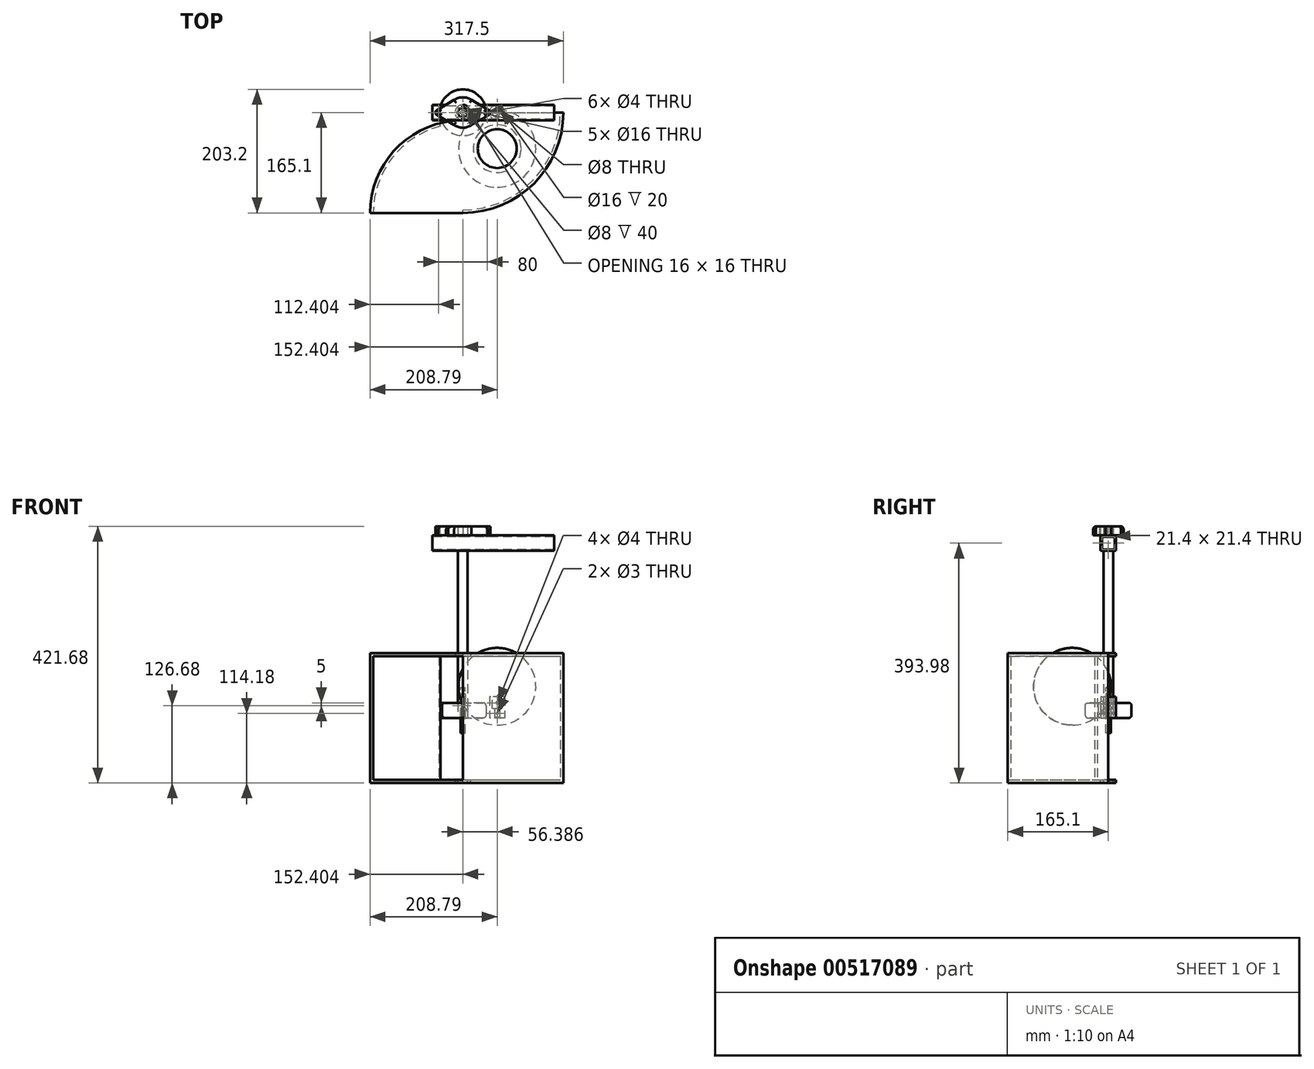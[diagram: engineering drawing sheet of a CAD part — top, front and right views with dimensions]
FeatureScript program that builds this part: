
annotation { "Feature Type Name" : "Feature", "Feature Type Description" : "" }
export const myFeature = defineFeature(function(context is Context, id is Id, definition is map)
    precondition{}
    {
        {
            var Q0;
            Q0=qCreatedBy(makeId("Top.planeOp"),FACE);
            var sketch = newSketch(context, id + "F0", { "sketchPlane" : qUnion([Q0])});
            skCircle(sketch, "E0", {"center": v(0, 0) * mm, "radius": 4 * mm});
            skCircle(sketch, "E1", {"center": v(0, 0) * mm, "radius": 12.5 * mm});
            skSolve(sketch);
        }
        {
            var Q0;
            Q0 = qSketchRegion(id + "F0", true);
            extrude(context, id + "F1", {"entities" : qUnion([Q0]), "depth" : 35 * mm, "offsetDistance" : 25 * mm});
        }
        {
            var Q0;
            Q0=makeQuery(id+"F1.opExtrude","CAP_FACE",FACE,{"disambiguationData":[OSD([sQuery(id+"F0.wireOp",EDGE,"E0"),sQuery(id+"F0.wireOp",EDGE,"E1")])],"isStart":false});
            var sketch = newSketch(context, id + "F2", { "sketchPlane" : qUnion([Q0])});
            skCircle(sketch, "E2", {"center": v(0, 0) * mm, "radius": 8 * mm});
            skSolve(sketch);
        }
        {
            var Q0;
            Q0 = qSketchRegion(id + "F2", true);
            extrude(context, id + "F3", {"entities" : qUnion([Q0]), "operationType" : NewBodyOperationType.REMOVE, "oppositeDirection" : true, "depth" : 20 * mm, "offsetDistance" : 25 * mm});
        }
        {
            var Q0;
            Q0=qCreatedBy(makeId("Right.planeOp"),FACE);
            cPlane(context, id + "F4", {"entities" : qUnion([Q0]), "cplaneType" : CPlaneType.OFFSET, "offset" : 0 * mm, "width" : 150 * mm, "height" : 150 * mm});
        }
        {
            var Q0;
            Q0=qCreatedBy(makeId("Front.planeOp"),FACE);
            var sketch = newSketch(context, id + "F5", { "sketchPlane" : qUnion([Q0])});
            skLineSegment(sketch, "E3.0", {"start": v(-12.5, 35) * mm, "end": v(12.5, 35) * mm});
            skLineSegment(sketch, "E4.0", {"start": v(-4, 0) * mm, "end": v(4, 0) * mm});
            skLineSegment(sketch, "E5", {"start": v(0, 0) * mm, "end": v(0, 35) * mm});
            skLineSegment(sketch, "E6", {"start": v(0, 35) * mm, "end": v(0, 25) * mm});
            skLineSegment(sketch, "E7", {"start": v(0, 0) * mm, "end": v(0, 7.5) * mm});
            skCircle(sketch, "E8", {"center": v(0, 7.5) * mm, "radius": 1.5 * mm});
            skCircle(sketch, "E9", {"center": v(0, 25) * mm, "radius": 2 * mm});
            skSolve(sketch);
        }
        {
            var Q0;
            Q0 = qSketchRegion(id + "F5", true);
            extrude(context, id + "F6", {"entities" : qUnion([Q0]), "operationType" : NewBodyOperationType.REMOVE, "oppositeDirection" : true, "depth" : 25 * mm, "offsetDistance" : 25 * mm, "hasSecondDirection" : true, "secondDirectionOppositeDirection" : false, "secondDirectionDepth" : 25 * mm});
        }
        {
            var Q0;
            Q0=makeQuery(id+"F1.opExtrude","CAP_EDGE",EDGE,{"disambiguationData":[OSD([sQuery(id+"F0.wireOp",EDGE,"E0")])],"isStart":true});
            var Q1;
            Q1=makeQuery(id+"F3.boolean.opBoolean","COPY",EDGE,{"derivedFrom":makeQuery(id+"F3.opExtrude","CAP_EDGE",EDGE,{"disambiguationData":[OSD([sQuery(id+"F2.wireOp",EDGE,"E2")])],"isStart":true})});
            chamfer(context, id + "F7", {"entities" : qUnion([Q0, Q1]), "width" : 1 * mm, "tangentPropagation" : true});
        }
        {
            var Q0;
            Q0=qCreatedBy(makeId("Top.planeOp"),FACE);
            var sketch = newSketch(context, id + "F8", { "sketchPlane" : qUnion([Q0])});
            skCircle(sketch, "E10", {"center": v(-56.39, 0) * mm, "radius": 8 * mm});
            skSolve(sketch);
        }
        {
            var Q0;
            Q0 = qSketchRegion(id + "F8", true);
            extrude(context, id + "F9", {"entities" : qUnion([Q0]), "depth" : 300 * mm, "offsetDistance" : 25 * mm});
        }
        {
            var Q0;
            Q0=makeQuery(id+"F9.opExtrude","CAP_FACE",FACE,{"disambiguationData":[OSD([sQuery(id+"F8.wireOp",EDGE,"E10")])],"isStart":true});
            var sketch = newSketch(context, id + "F10", { "sketchPlane" : qUnion([Q0])});
            skCircle(sketch, "E11", {"center": v(-56.39, 0) * mm, "radius": 4 * mm});
            skSolve(sketch);
        }
        {
            var Q0;
            Q0 = qSketchRegion(id + "F10", true);
            extrude(context, id + "F11", {"entities" : qUnion([Q0]), "operationType" : NewBodyOperationType.REMOVE, "oppositeDirection" : true, "depth" : 40 * mm, "offsetDistance" : 25 * mm});
        }
        {
            var Q0;
            Q0=qCreatedBy(makeId("Front.planeOp"),FACE);
            var sketch = newSketch(context, id + "F12", { "sketchPlane" : qUnion([Q0])});
            skLineSegment(sketch, "E12.0", {"start": v(-64.39, 0) * mm, "end": v(-48.39, 0) * mm});
            skLineSegment(sketch, "E13", {"start": v(-56.39, 0) * mm, "end": v(-56.39, 20) * mm});
            skCircle(sketch, "E14", {"center": v(-56.39, 20) * mm, "radius": 2 * mm});
            skSolve(sketch);
        }
        {
            var Q0;
            Q0 = qSketchRegion(id + "F12", true);
            extrude(context, id + "F13", {"entities" : qUnion([Q0]), "operationType" : NewBodyOperationType.REMOVE, "oppositeDirection" : true, "depth" : 25 * mm, "offsetDistance" : 25 * mm, "hasSecondDirection" : true, "secondDirectionOppositeDirection" : false, "secondDirectionDepth" : 25 * mm});
        }
        {
            var Q0;
            Q0=makeQuery(id+"F9.opExtrude","CAP_FACE",FACE,{"disambiguationData":[OSD([sQuery(id+"F8.wireOp",EDGE,"E10")])],"isStart":true});
            var sketch = newSketch(context, id + "F14", { "sketchPlane" : qUnion([Q0])});
            skCircle(sketch, "E15", {"center": v(-56.39, 0) * mm, "radius": 3.94 * mm});
            skSolve(sketch);
        }
        {
            var Q0;
            Q0 = qSketchRegion(id + "F14", true);
            extrude(context, id + "F15", {"entities" : qUnion([Q0]), "depth" : 25 * mm, "offsetDistance" : 25 * mm, "hasSecondDirection" : true, "secondDirectionOppositeDirection" : true, "secondDirectionDepth" : 50 * mm});
        }
        {
            var Q0;
            Q0=qCreatedBy(makeId("Top.planeOp"),FACE);
            var sketch = newSketch(context, id + "F16", { "sketchPlane" : qUnion([Q0])});
            skCircle(sketch, "E16.0", {"center": v(-56.39, 0) * mm, "radius": 8 * mm});
            skCircle(sketch, "E17", {"center": v(-56.39, 0) * mm, "radius": 38.1 * mm});
            skSolve(sketch);
        }
        {
            var Q0;
            Q0 = qSketchRegion(id + "F16", true);
            extrude(context, id + "F17", {"entities" : qUnion([Q0]), "depth" : 25 * mm, "offsetDistance" : 25 * mm});
        }
        {
            var Q0;
            Q0=makeQuery(id+"F17.opExtrude","CAP_EDGE",EDGE,{"disambiguationData":[OSD([sQuery(id+"F16.wireOp",EDGE,"E17")])],"isStart":false});
            var Q1;
            Q1=makeQuery(id+"F17.opExtrude","CAP_EDGE",EDGE,{"disambiguationData":[OSD([sQuery(id+"F16.wireOp",EDGE,"E17")])],"isStart":true});
            fillet(context, id + "F18", {"entities" : qUnion([Q0, Q1]), "radius" : 5 * mm, "tangentPropagation" : true, "allowEdgeOverflow" : false});
        }
        {
            var Q0;
            Q0=makeQuery(id+"F9.opExtrude","CAP_FACE",FACE,{"disambiguationData":[OSD([sQuery(id+"F8.wireOp",EDGE,"E10")])],"isStart":false});
            var sketch = newSketch(context, id + "F19", { "sketchPlane" : qUnion([Q0])});
            skCircle(sketch, "E18.0", {"center": v(-56.39, 0) * mm, "radius": 8 * mm});
            skCircle(sketch, "E19", {"center": v(-56.39, 0) * mm, "radius": 13.3 * mm});
            skLineSegment(sketch, "E20", {"start": v(-56.39, 0) * mm, "end": v(-96.39, 0) * mm});
            skLineSegment(sketch, "E21", {"start": v(-96.39, 0) * mm, "end": v(-56.39, 0) * mm});
            skLineSegment(sketch, "E22", {"start": v(-56.39, 0) * mm, "end": v(-16.39, 0) * mm});
            skCircle(sketch, "E23", {"center": v(-16.39, 0) * mm, "radius": 5 * mm});
            skCircle(sketch, "E24", {"center": v(-96.39, 0) * mm, "radius": 5 * mm});
            skCircle(sketch, "E25", {"center": v(-56.39, 0) * mm, "radius": 25 * mm});
            skLineSegment(sketch, "E26", {"start": v(-42.15, -20.55) * mm, "end": v(-15.67, -4.95) * mm});
            skLineSegment(sketch, "E27", {"start": v(-56.39, 0) * mm, "end": v(-56.39, -25) * mm});
            skLineSegment(sketch, "E28.MirrorCS", {"start": v(-70.62, -20.55) * mm, "end": v(-97.1, -4.95) * mm});
            skLineSegment(sketch, "E29.MirrorCS", {"start": v(-70.62, 20.55) * mm, "end": v(-97.1, 4.95) * mm});
            skLineSegment(sketch, "E30.MirrorCS", {"start": v(-42.15, 20.55) * mm, "end": v(-15.67, 4.95) * mm});
            skCircle(sketch, "E31", {"center": v(-16.39, 0) * mm, "radius": 2 * mm});
            skCircle(sketch, "E32", {"center": v(-96.39, 0) * mm, "radius": 2 * mm});
            skSolve(sketch);
        }
        {
            var Q0;
            Q0 = qSketchRegion(id + "F19", true);
            var Q1;
            {var subQ0=sQuery(id+"F19.wireOp",EDGE,"E21");var subQ1=sQuery(id+"F19.wireOp",EDGE,"E18.0");var subQ2=makeQuery(id+"F19.imprint","INTERSECT",VERTEX,{"derivedFrom":[subQ1,subQ0]});Q1=makeQuery(id+"F19.imprint","IMPRINT",FACE,{"disambiguationData":[TD([[makeQuery(id+"F19.imprint","IMPRINT",EDGE,{"disambiguationData":[TD([[subQ2,-1.0]])],"derivedFrom":subQ1}),-1.0]])]});}
            var Q2;
            {var subQ0=sQuery(id+"F19.wireOp",EDGE,"E21");var subQ1=sQuery(id+"F19.wireOp",EDGE,"E18.0");var subQ2=makeQuery(id+"F19.imprint","INTERSECT",VERTEX,{"derivedFrom":[subQ1,subQ0]});Q2=makeQuery(id+"F19.imprint","IMPRINT",FACE,{"disambiguationData":[TD([[makeQuery(id+"F19.imprint","IMPRINT",EDGE,{"disambiguationData":[TD([[subQ2,1.0]])],"derivedFrom":subQ1}),-1.0]])]});}
            var Q3;
            {var subQ0=sQuery(id+"F19.wireOp",EDGE,"E22");var subQ1=sQuery(id+"F19.wireOp",EDGE,"E18.0");var subQ2=makeQuery(id+"F19.imprint","INTERSECT",VERTEX,{"derivedFrom":[subQ1,subQ0]});Q3=makeQuery(id+"F19.imprint","IMPRINT",FACE,{"disambiguationData":[TD([[makeQuery(id+"F19.imprint","IMPRINT",EDGE,{"disambiguationData":[TD([[subQ2,1.0]])],"derivedFrom":subQ1}),-1.0]])]});}
            extrude(context, id + "F20", {"entities" : qUnion([Q0, Q1, Q2, Q3]), "depth" : 15 * mm, "offsetDistance" : 25 * mm});
        }
        {
            var Q0;
            Q0=makeQuery(id+"F20.opExtrude","CAP_EDGE",EDGE,{"disambiguationData":[OSD([sQuery(id+"F19.wireOp",EDGE,"E28.MirrorCS")])],"isStart":false});
            var Q1;
            Q1=makeQuery(id+"F20.opExtrude","CAP_EDGE",EDGE,{"disambiguationData":[OSD([sQuery(id+"F19.wireOp",EDGE,"E26")])],"isStart":false});
            var Q2;
            Q2=makeQuery(id+"F20.opExtrude","CAP_EDGE",EDGE,{"disambiguationData":[OSD([sQuery(id+"F19.wireOp",EDGE,"E30.MirrorCS")])],"isStart":false});
            var Q3;
            Q3=makeQuery(id+"F20.opExtrude","CAP_EDGE",EDGE,{"disambiguationData":[OSD([sQuery(id+"F19.wireOp",EDGE,"E29.MirrorCS")])],"isStart":false});
            var Q4;
            {var subQ0=sQuery(id+"F19.wireOp",EDGE,"E25");Q4=makeQuery(id+"F20.opExtrude","CAP_EDGE",EDGE,{"disambiguationData":[OSD([subQ0]),TDD([makeQuery(id+"F19.imprint","IMPRINT",EDGE,{"disambiguationData":[TD([[makeQuery(id+"F19.imprint","INTERSECT",VERTEX,{"derivedFrom":[subQ0,sQuery(id+"F19.wireOp",EDGE,"E29.MirrorCS")]}),1.0]])],"derivedFrom":subQ0})])],"isStart":false});}
            var Q5;
            {var subQ0=sQuery(id+"F19.wireOp",EDGE,"E25");var subQ1=makeQuery(id+"F19.imprint","INTERSECT",VERTEX,{"derivedFrom":[subQ0,sQuery(id+"F19.wireOp",EDGE,"E27")]});Q5=makeQuery(id+"F20.opExtrude","CAP_EDGE",EDGE,{"disambiguationData":[OSD([subQ0]),TDD([makeQuery(id+"F19.imprint","IMPRINT",EDGE,{"disambiguationData":[TD([[subQ1,1.0]])],"derivedFrom":subQ0}),makeQuery(id+"F19.imprint","IMPRINT",EDGE,{"disambiguationData":[TD([[makeQuery(id+"F19.imprint","INTERSECT",VERTEX,{"derivedFrom":[subQ0,sQuery(id+"F19.wireOp",EDGE,"E26")]}),1.0]])],"derivedFrom":subQ0})])],"isStart":false});}
            fillet(context, id + "F21", {"entities" : qUnion([Q0, Q1, Q2, Q3, Q4, Q5]), "radius" : 5 * mm, "tangentPropagation" : true, "allowEdgeOverflow" : false});
        }
        {
            var Q0;
            Q0=makeQuery(id+"F20.opExtrude","CAP_FACE",FACE,{"disambiguationData":[OSD([sQuery(id+"F19.wireOp",EDGE,"E18.0"),sQuery(id+"F19.wireOp",EDGE,"E23"),sQuery(id+"F19.wireOp",EDGE,"E24"),sQuery(id+"F19.wireOp",EDGE,"E25"),sQuery(id+"F19.wireOp",EDGE,"E26"),sQuery(id+"F19.wireOp",EDGE,"E28.MirrorCS"),sQuery(id+"F19.wireOp",EDGE,"E29.MirrorCS"),sQuery(id+"F19.wireOp",EDGE,"E30.MirrorCS"),sQuery(id+"F19.wireOp",EDGE,"E31"),sQuery(id+"F19.wireOp",EDGE,"E32")])],"isStart":true});
            var sketch = newSketch(context, id + "F22", { "sketchPlane" : qUnion([Q0])});
            skCircle(sketch, "E33.0", {"center": v(-56.39, 0) * mm, "radius": 8 * mm});
            skLineSegment(sketch, "E34.bottom", {"start": v(-6.39, 12.7) * mm, "end": v(-106.39, 12.7) * mm});
            skLineSegment(sketch, "E34.top", {"start": v(-6.39, -12.7) * mm, "end": v(-106.39, -12.7) * mm});
            skLineSegment(sketch, "E34.right", {"start": v(-106.39, 12.7) * mm, "end": v(-106.39, -12.7) * mm});
            skLineSegment(sketch, "E35", {"start": v(-6.39, -12.7) * mm, "end": v(93.61, -12.7) * mm});
            skLineSegment(sketch, "E36", {"start": v(93.61, -12.7) * mm, "end": v(93.61, 12.7) * mm});
            skLineSegment(sketch, "E37", {"start": v(93.61, 12.7) * mm, "end": v(-6.39, 12.7) * mm});
            skCircle(sketch, "E38.0", {"center": v(-96.39, 0) * mm, "radius": 2 * mm});
            skCircle(sketch, "E39.0", {"center": v(-16.39, 0) * mm, "radius": 2 * mm});
            skSolve(sketch);
        }
        {
            var Q0;
            Q0 = qSketchRegion(id + "F22", true);
            extrude(context, id + "F23", {"entities" : qUnion([Q0]), "depth" : 25.4 * mm, "offsetDistance" : 25 * mm});
        }
        {
            var Q0;
            Q0=makeQuery(id+"F23.opExtrude","SWEPT_FACE",FACE,{"disambiguationData":[OSD([sQuery(id+"F22.wireOp",EDGE,"E34.right")])]});
            var sketch = newSketch(context, id + "F24", { "sketchPlane" : qUnion([Q0])});
            skLineSegment(sketch, "E40.0", {"start": v(10.7, 298) * mm, "end": v(-10.7, 298) * mm});
            skLineSegment(sketch, "E40.1", {"start": v(10.7, 276.6) * mm, "end": v(10.7, 298) * mm});
            skLineSegment(sketch, "E40.2", {"start": v(-10.7, 276.6) * mm, "end": v(10.7, 276.6) * mm});
            skLineSegment(sketch, "E40.3", {"start": v(-10.7, 298) * mm, "end": v(-10.7, 276.6) * mm});
            skSolve(sketch);
        }
        {
            var Q0;
            Q0 = qSketchRegion(id + "F24", true);
            extrude(context, id + "F25", {"entities" : qUnion([Q0]), "operationType" : NewBodyOperationType.REMOVE, "oppositeDirection" : true, "depth" : 500 * mm, "offsetDistance" : 25 * mm});
        }
        {
            var Q0;
            Q0=qCreatedBy(id+"F4.planeOp",FACE);
            var sketch = newSketch(context, id + "F26", { "sketchPlane" : qUnion([Q0])});
            skCircle(sketch, "E41", {"center": v(-59.35, 51.77) * mm, "radius": 63.5 * mm});
            skLineSegment(sketch, "E42", {"start": v(-59.35, 115.27) * mm, "end": v(-59.35, -11.73) * mm});
            skSolve(sketch);
        }
        {
            var Q0;
            {var subQ0=sQuery(id+"F26.wireOp",EDGE,"E42");Q0=makeQuery(id+"F26.imprint","IMPRINT",FACE,{"disambiguationData":[TD([[makeQuery(id+"F26.imprint","IMPRINT",EDGE,{"derivedFrom":subQ0}),1.0]])]});}
            var Q1;
            Q1=sQuery(id+"F26.wireOp",EDGE,"E42");
            revolve(context, id + "F27", {"entities" : qUnion([Q0]), "axis" : qUnion([Q1]), "revolveType" : RevolveType.FULL});
        }
        {
            var Q0;
            Q0=qCreatedBy(makeId("Top.planeOp"),FACE);
            var sketch = newSketch(context, id + "F28", { "sketchPlane" : qUnion([Q0])});
            skCircle(sketch, "E43.0", {"center": v(-56.39, 0) * mm, "radius": 38.1 * mm});
            skArc(sketch, "E44", {"start": v(-56.39, -160.02) * mm, "mid": v(56.77, -113.15) * mm, "end": v(103.63, 0) * mm});
            skArc(sketch, "E45.0", {"start": v(-56.39, -165.1) * mm, "mid": v(60.36, -116.74) * mm, "end": v(108.71, 0) * mm});
            skLineSegment(sketch, "E46", {"start": v(-56.39, 0) * mm, "end": v(-56.39, -211.07) * mm});
            skLineSegment(sketch, "E47", {"start": v(-56.39, 0) * mm, "end": v(143.2, 0) * mm});
            skSolve(sketch);
        }
        {
            var Q0;
            {var subQ0=sQuery(id+"F28.wireOp",EDGE,"E44");Q0=makeQuery(id+"F28.imprint","IMPRINT",FACE,{"disambiguationData":[TD([[makeQuery(id+"F28.imprint","IMPRINT",EDGE,{"derivedFrom":subQ0}),-1.0]])]});}
            extrude(context, id + "F29", {"entities" : qUnion([Q0]), "depth" : 101.6 * mm, "offsetDistance" : 25 * mm, "hasSecondDirection" : true, "secondDirectionOppositeDirection" : true, "secondDirectionDepth" : 101.6 * mm});
        }
        {
            var Q0;
            Q0=makeQuery(id+"F29.opExtrude","CAP_FACE",FACE,{"disambiguationData":[OSD([sQuery(id+"F28.wireOp",EDGE,"E44"),sQuery(id+"F28.wireOp",EDGE,"E45.0"),sQuery(id+"F28.wireOp",EDGE,"E46"),sQuery(id+"F28.wireOp",EDGE,"E47")])],"isStart":true});
            var sketch = newSketch(context, id + "F30", { "sketchPlane" : qUnion([Q0])});
            skCircle(sketch, "E48.0", {"center": v(-56.39, 0) * mm, "radius": 3.94 * mm});
            skLineSegment(sketch, "E49", {"start": v(-56.39, 0) * mm, "end": v(-56.39, 160.02) * mm});
            skLineSegment(sketch, "E50", {"start": v(-56.39, 0) * mm, "end": v(108.71, 0) * mm});
            skArc(sketch, "E51.0", {"start": v(-56.39, 160.02) * mm, "mid": v(56.77, 113.15) * mm, "end": v(103.63, 0) * mm});
            skArc(sketch, "E52.0", {"start": v(-56.39, 165.1) * mm, "mid": v(60.36, 116.74) * mm, "end": v(108.71, 0) * mm});
            skCircle(sketch, "E53", {"center": v(-56.39, 0) * mm, "radius": 12.7 * mm});
            skCircle(sketch, "E54.0", {"center": v(-56.39, 0) * mm, "radius": 8 * mm});
            skSolve(sketch);
        }
        {
            var Q0;
            Q0 = qSketchRegion(id + "F30", true);
            var Q1;
            {var subQ0=sQuery(id+"F30.wireOp",EDGE,"E51.0");Q1=makeQuery(id+"F30.imprint","IMPRINT",FACE,{"disambiguationData":[TD([[makeQuery(id+"F30.imprint","IMPRINT",EDGE,{"derivedFrom":subQ0}),1.0]])]});}
            extrude(context, id + "F31", {"entities" : qUnion([Q0, Q1]), "operationType" : NewBodyOperationType.ADD, "depth" : 5.08 * mm, "offsetDistance" : 25 * mm});
        }
        {
            var Q0;
            Q0=makeQuery(id+"F29.opExtrude","CAP_FACE",FACE,{"disambiguationData":[OSD([sQuery(id+"F28.wireOp",EDGE,"E44"),sQuery(id+"F28.wireOp",EDGE,"E45.0"),sQuery(id+"F28.wireOp",EDGE,"E46"),sQuery(id+"F28.wireOp",EDGE,"E47")])],"isStart":false});
            var sketch = newSketch(context, id + "F32", { "sketchPlane" : qUnion([Q0])});
            skLineSegment(sketch, "E55.0.0", {"start": v(-56.39, -12.7) * mm, "end": v(-56.39, -160.02) * mm});
            skArc(sketch, "E55.0.1", {"start": v(-56.39, -160.02) * mm, "mid": v(56.77, -113.15) * mm, "end": v(103.63, 0) * mm});
            skLineSegment(sketch, "E55.0.2", {"start": v(103.63, 0) * mm, "end": v(-43.69, 0) * mm});
            skArc(sketch, "E55.0.3", {"start": v(-43.69, 0) * mm, "mid": v(-65.37, 8.98) * mm, "end": v(-56.39, -12.7) * mm});
            skArc(sketch, "E56.0", {"start": v(-56.39, -165.1) * mm, "mid": v(60.36, -116.74) * mm, "end": v(108.71, 0) * mm});
            skLineSegment(sketch, "E57.0", {"start": v(-56.39, -160.02) * mm, "end": v(-56.39, -165.1) * mm});
            skLineSegment(sketch, "E58.0", {"start": v(103.63, 0) * mm, "end": v(108.71, 0) * mm});
            skCircle(sketch, "E59.0", {"center": v(-56.39, 0) * mm, "radius": 8 * mm});
            skSolve(sketch);
        }
        {
            var Q0;
            Q0 = qSketchRegion(id + "F32", true);
            extrude(context, id + "F33", {"entities" : qUnion([Q0]), "operationType" : NewBodyOperationType.ADD, "depth" : 5.08 * mm, "offsetDistance" : 25 * mm});
        }
        {
            var Q0;
            {var subQ0=sQuery(id+"F28.wireOp",EDGE,"E46");Q0=makeQuery(id+"F33.boolean.opBoolean","MERGE",FACE,{"derivedFrom":[makeQuery(id+"F31.boolean.opBoolean","MERGE",FACE,{"derivedFrom":[makeQuery(id+"F29.opExtrude","SWEPT_FACE",FACE,{"disambiguationData":[OSD([subQ0])]}),makeQuery(id+"F31.opExtrude","SWEPT_FACE",FACE,{"disambiguationData":[OSD([subQ0,sQuery(id+"F30.wireOp",EDGE,"E49")])]})]}),makeQuery(id+"F33.opExtrude","SWEPT_FACE",FACE,{"disambiguationData":[OSD([sQuery(id+"F32.wireOp",EDGE,"E55.0.0"),sQuery(id+"F32.wireOp",EDGE,"E57.0")])]})]});}
            extrude(context, id + "F34", {"entities" : qUnion([Q0]), "operationType" : NewBodyOperationType.ADD, "depth" : 152.4 * mm, "offsetDistance" : 25 * mm});
        }
        {
            var Q0;
            {var subQ0=sQuery(id+"F30.wireOp",EDGE,"E49");var subQ1=sQuery(id+"F28.wireOp",EDGE,"E46");Q0=makeQuery(id+"F34.boolean.opBoolean","MERGE",FACE,{"derivedFrom":[makeQuery(id+"F31.opExtrude","CAP_FACE",FACE,{"disambiguationData":[OSD([subQ1,subQ0,sQuery(id+"F30.wireOp",EDGE,"E50"),sQuery(id+"F30.wireOp",EDGE,"E52.0"),sQuery(id+"F30.wireOp",EDGE,"E53"),sQuery(id+"F30.wireOp",EDGE,"E54.0")])],"isStart":false}),makeQuery(id+"F34.opExtrude","SWEPT_FACE",FACE,{"disambiguationData":[OSD([subQ1,subQ0]),TDD([makeQuery(id+"F31.opExtrude","CAP_EDGE",EDGE,{"disambiguationData":[OSD([subQ1,subQ0])],"isStart":false})])]})]});}
            var sketch = newSketch(context, id + "F35", { "sketchPlane" : qUnion([Q0])});
            skArc(sketch, "E60.0", {"start": v(-56.39, 12.7) * mm, "mid": v(-65.37, -8.98) * mm, "end": v(-43.69, 0) * mm});
            skLineSegment(sketch, "E61", {"start": v(-56.39, 12.7) * mm, "end": v(-56.39, 203.81) * mm});
            skCircle(sketch, "E62", {"center": v(-56.39, 165.1) * mm, "radius": 152.4 * mm});
            skSolve(sketch);
        }
        {
            var Q0;
            {var subQ1=sQuery(id+"F30.wireOp",EDGE,"E49");var subQ4=sQuery(id+"F30.wireOp",EDGE,"E53");var subQ5=makeQuery(id+"F34.opExtrude","SWEPT_EDGE",EDGE,{"disambiguationData":[OSD([subQ1,subQ4]),TDD([makeQuery(id+"F31.opExtrude","CAP_VERTEX",VERTEX,{"disambiguationData":[OSD([subQ1,subQ4])],"isStart":false})])]});Q0=makeQuery(id+"F35.imprint","IMPRINT",FACE,{"disambiguationData":[TD([[makeQuery(id+"F35.imprint","IMPRINT",EDGE,{"derivedFrom":subQ5}),1.0]])]});}
            extrude(context, id + "F36", {"entities" : qUnion([Q0]), "operationType" : NewBodyOperationType.REMOVE, "oppositeDirection" : true, "depth" : 1270 * mm, "offsetDistance" : 25 * mm});
        }
        {
            var Q0;
            Q0=makeQuery(id+"F34.opExtrude","SWEPT_FACE",FACE,{"disambiguationData":[OSD([sQuery(id+"F28.wireOp",EDGE,"E44"),sQuery(id+"F28.wireOp",EDGE,"E46")])]});
            var sketch = newSketch(context, id + "F37", { "sketchPlane" : qUnion([Q0])});
            skSolve(sketch);
        }
        {
            var Q0;
            {var subQ0=sQuery(id+"F28.wireOp",EDGE,"E46");var subQ1=sQuery(id+"F28.wireOp",EDGE,"E44");Q0=makeQuery(id+"F37.imprint","IMPRINT",FACE,{"disambiguationData":[TD([[makeQuery(id+"F37.imprint","IMPRINT",EDGE,{"derivedFrom":makeQuery(id+"F34.opExtrude","SWEPT_EDGE",EDGE,{"disambiguationData":[OSD([subQ1,subQ0]),TDD([makeQuery(id+"F29.opExtrude","CAP_VERTEX",VERTEX,{"disambiguationData":[OSD([subQ1,subQ0])],"isStart":true})])]})}),-1.0]])]});}
            extrude(context, id + "F38", {"entities" : qUnion([Q0]), "operationType" : NewBodyOperationType.REMOVE, "oppositeDirection" : true, "depth" : 25 * mm, "offsetDistance" : 25 * mm});
        }
        {
            var Q0;
            {var subQ0=sQuery(id+"F30.wireOp",EDGE,"E49");var subQ1=sQuery(id+"F28.wireOp",EDGE,"E46");Q0=makeQuery(id+"F34.boolean.opBoolean","MERGE",FACE,{"derivedFrom":[makeQuery(id+"F31.opExtrude","CAP_FACE",FACE,{"disambiguationData":[OSD([subQ1,subQ0,sQuery(id+"F30.wireOp",EDGE,"E50"),sQuery(id+"F30.wireOp",EDGE,"E52.0"),sQuery(id+"F30.wireOp",EDGE,"E53"),sQuery(id+"F30.wireOp",EDGE,"E54.0")])],"isStart":false}),makeQuery(id+"F34.opExtrude","SWEPT_FACE",FACE,{"disambiguationData":[OSD([subQ1,subQ0]),TDD([makeQuery(id+"F31.opExtrude","CAP_EDGE",EDGE,{"disambiguationData":[OSD([subQ1,subQ0])],"isStart":false})])]})]});}
            var sketch = newSketch(context, id + "F39", { "sketchPlane" : qUnion([Q0])});
            skCircle(sketch, "E63.0", {"center": v(-56.39, 0) * mm, "radius": 38.1 * mm});
            skArc(sketch, "E64.0", {"start": v(-208.79, 165.1) * mm, "mid": v(-164.15, 57.34) * mm, "end": v(-56.39, 12.7) * mm});
            skArc(sketch, "E65.0", {"start": v(-203.7, 165.1) * mm, "mid": v(-160.56, 60.93) * mm, "end": v(-56.39, 17.78) * mm});
            skCircle(sketch, "E66.0", {"center": v(-56.39, 0) * mm, "radius": 43.1 * mm});
            skSolve(sketch);
        }
        {
            var Q0;
            {var subQ0=sQuery(id+"F39.wireOp",EDGE,"E64.0");var subQ3=sQuery(id+"F39.wireOp",EDGE,"E66.0");var subQ4=makeQuery(id+"F39.imprint","INTERSECT",VERTEX,{"derivedFrom":[subQ0,subQ3]});Q0=makeQuery(id+"F39.imprint","IMPRINT",FACE,{"disambiguationData":[TD([[makeQuery(id+"F39.imprint","IMPRINT",EDGE,{"disambiguationData":[TD([[subQ4,1.0]])],"derivedFrom":subQ3}),-1.0]])]});}
            var Q1;
            {var subQ0=sQuery(id+"F32.wireOp",EDGE,"E57.0");var subQ1=sQuery(id+"F32.wireOp",EDGE,"E55.0.0");Q1=makeQuery(id+"F34.boolean.opBoolean","MERGE",FACE,{"derivedFrom":[makeQuery(id+"F33.opExtrude","CAP_FACE",FACE,{"disambiguationData":[OSD([subQ1,sQuery(id+"F32.wireOp",EDGE,"E55.0.2"),sQuery(id+"F32.wireOp",EDGE,"E55.0.3"),sQuery(id+"F32.wireOp",EDGE,"E56.0"),subQ0,sQuery(id+"F32.wireOp",EDGE,"E58.0"),sQuery(id+"F32.wireOp",EDGE,"E59.0")])],"isStart":false}),makeQuery(id+"F34.opExtrude","SWEPT_FACE",FACE,{"disambiguationData":[OSD([subQ1,subQ0]),TDD([makeQuery(id+"F33.opExtrude","CAP_EDGE",EDGE,{"disambiguationData":[OSD([subQ1,subQ0])],"isStart":false})])]})]});}
            extrude(context, id + "F40", {"entities" : qUnion([Q0]), "operationType" : NewBodyOperationType.ADD, "endBound" : BoundingType.UP_TO_SURFACE, "oppositeDirection" : true, "depth" : 25 * mm, "endBoundEntityFace" : qUnion([Q1]), "offsetDistance" : 25 * mm});
        }
    });
